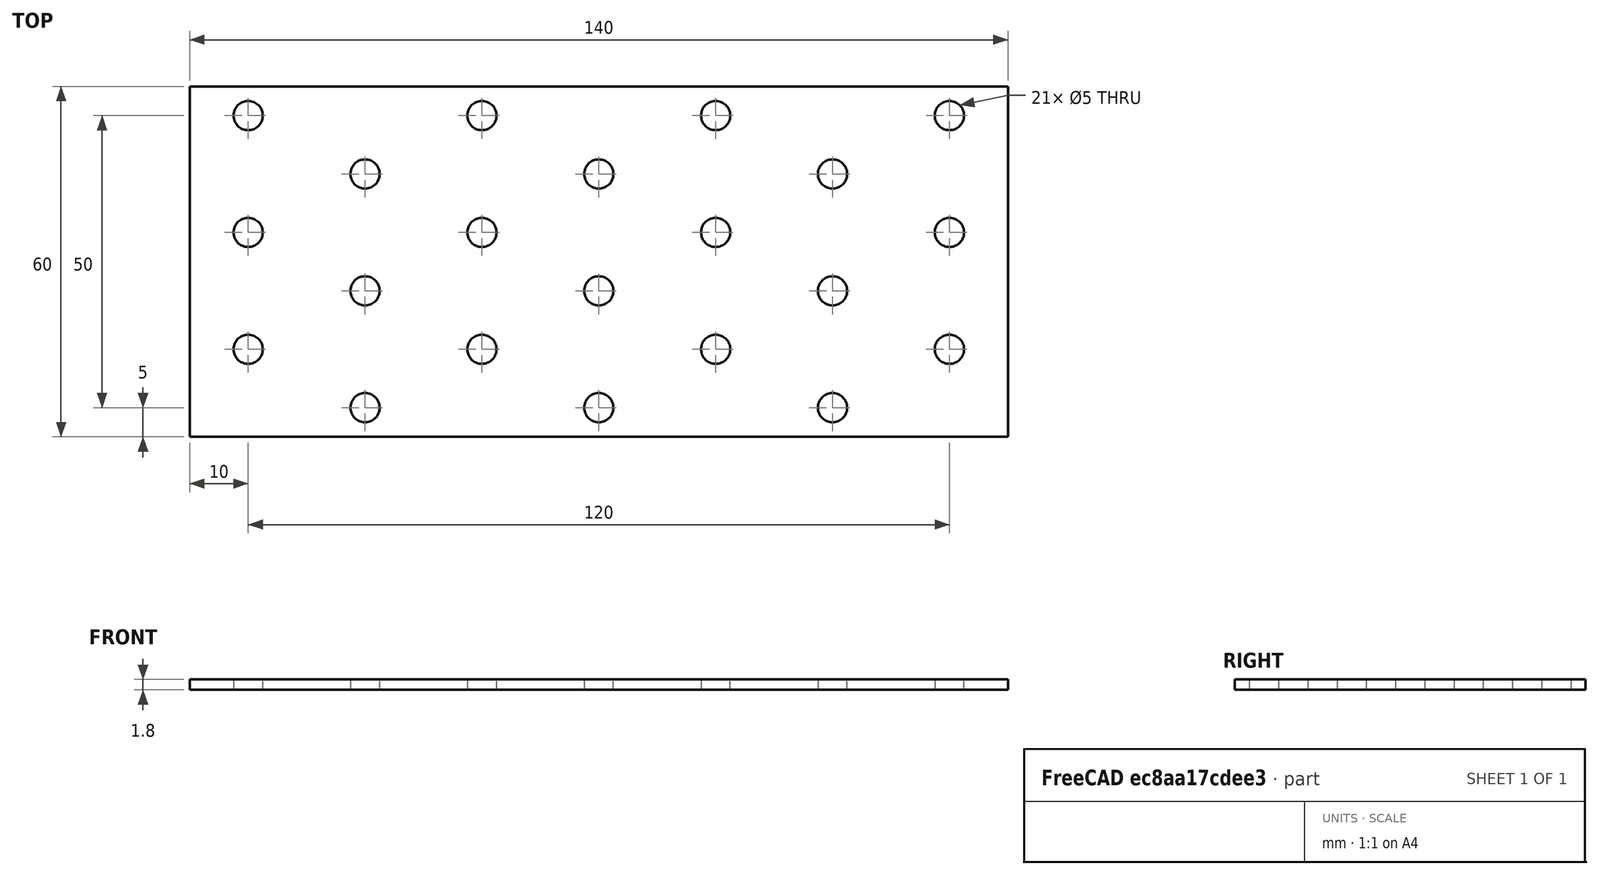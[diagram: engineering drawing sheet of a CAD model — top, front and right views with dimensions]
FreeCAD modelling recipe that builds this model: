
FCSTD DOCUMENT  (FreeCAD 0.19R24276 (Git))
Label: Bar_60x140__1_8mm_for-kern_endpoint_plate
License: All rights reserved
LicenseURL: http://en.wikipedia.org/wiki/All_rights_reserved
objects: Sketcher::SketchObject×1, PartDesign::Pad×1, PartDesign::Body×1
note: 4 computed .brp shape members not serialized (recipe doc carries the construction recipe); baked Part::Feature solids carry a one-line shape summary decoded from their .brp

FEATURE [Sketcher::SketchObject] Sketch
  FullyConstrained = false
  MapMode = 5
  Support = -> [XY_Plane]
  sketch-geometry (56):
    g0: LineSegment StartX=0 StartY=0 StartZ=0 EndX=120 EndY=0 EndZ=0
    g1: LineSegment StartX=120 StartY=0 StartZ=0 EndX=120 EndY=80 EndZ=0
    g2: LineSegment StartX=120 StartY=80 StartZ=0 EndX=0 EndY=80 EndZ=0
    g3: LineSegment StartX=0 StartY=80 StartZ=0 EndX=0 EndY=0 EndZ=0
    g4: LineSegment StartX=0 StartY=4.5 StartZ=0 EndX=120 EndY=4.5 EndZ=0
    g5: LineSegment StartX=0 StartY=24.5 StartZ=0 EndX=120 EndY=24.5 EndZ=0
    g6: LineSegment StartX=0 StartY=44.5 StartZ=0 EndX=120 EndY=44.5 EndZ=0
    g7: LineSegment StartX=0 StartY=64.5 StartZ=0 EndX=120 EndY=64.5 EndZ=0
    g8: LineSegment StartX=48.5 StartY=0 StartZ=0 EndX=48.5 EndY=4.5 EndZ=0
    g9: LineSegment StartX=68.5 StartY=0 StartZ=0 EndX=68.5 EndY=4.5 EndZ=0
    g10: LineSegment StartX=88.5 StartY=0 StartZ=0 EndX=88.5 EndY=4.5 EndZ=0
    g11: LineSegment StartX=108.5 StartY=0 StartZ=0 EndX=108.5 EndY=4.5 EndZ=0
    g12: LineSegment StartX=0 StartY=14.5 StartZ=0 EndX=120 EndY=14.5 EndZ=0
    g13: LineSegment StartX=0 StartY=34.5 StartZ=0 EndX=120 EndY=34.5 EndZ=0
    g14: LineSegment StartX=0 StartY=54.5 StartZ=0 EndX=120 EndY=54.5 EndZ=0
    g15: LineSegment StartX=0 StartY=74.5 StartZ=0 EndX=120 EndY=74.5 EndZ=0
    g16: LineSegment StartX=48.5 StartY=24.5 StartZ=0 EndX=48.5 EndY=80 EndZ=0
    g17: LineSegment StartX=68.5 StartY=14.5 StartZ=0 EndX=68.5 EndY=80 EndZ=0
    g18: LineSegment StartX=88.5 StartY=24.5 StartZ=0 EndX=88.5 EndY=80 EndZ=0
    g19: LineSegment StartX=108.5 StartY=14.5 StartZ=0 EndX=108.5 EndY=80 EndZ=0
    g20: Circle CenterX=28.5 CenterY=14.5 CenterZ=0 NormalX=0 NormalY=0 NormalZ=1 AngleXU=0 Radius=2.5
    g21: Circle CenterX=108.5 CenterY=14.5 CenterZ=0 NormalX=0 NormalY=0 NormalZ=1 AngleXU=0 Radius=2.5
    g22: Circle CenterX=8.5 CenterY=24.5 CenterZ=0 NormalX=0 NormalY=0 NormalZ=1 AngleXU=0 Radius=2.5
    g23: Circle CenterX=48.5 CenterY=24.5 CenterZ=0 NormalX=0 NormalY=0 NormalZ=1 AngleXU=0 Radius=2.5
    g24: Circle CenterX=88.5 CenterY=24.5 CenterZ=0 NormalX=0 NormalY=0 NormalZ=1 AngleXU=0 Radius=2.5
    g25: Circle CenterX=8.5 CenterY=44.5 CenterZ=0 NormalX=0 NormalY=0 NormalZ=1 AngleXU=0 Radius=2.5
    g26: Circle CenterX=48.5 CenterY=44.5 CenterZ=0 NormalX=0 NormalY=0 NormalZ=1 AngleXU=0 Radius=2.5
    g27: Circle CenterX=88.5 CenterY=44.5 CenterZ=0 NormalX=0 NormalY=0 NormalZ=1 AngleXU=0 Radius=2.5
    g28: Circle CenterX=28.5 CenterY=54.5 CenterZ=0 NormalX=0 NormalY=0 NormalZ=1 AngleXU=0 Radius=2.5
    g29: Circle CenterX=68.5 CenterY=54.5 CenterZ=0 NormalX=0 NormalY=0 NormalZ=1 AngleXU=0 Radius=2.5
    g30: Circle CenterX=108.5 CenterY=54.5 CenterZ=0 NormalX=0 NormalY=0 NormalZ=1 AngleXU=0 Radius=2.5
    g31: Circle CenterX=88.5 CenterY=64.5 CenterZ=0 NormalX=0 NormalY=0 NormalZ=1 AngleXU=0 Radius=2.5
    g32: Circle CenterX=48.5 CenterY=64.5 CenterZ=0 NormalX=0 NormalY=0 NormalZ=1 AngleXU=0 Radius=2.5
    g33: Circle CenterX=8.5 CenterY=64.5 CenterZ=0 NormalX=0 NormalY=0 NormalZ=1 AngleXU=0 Radius=2.5
    g34: Circle CenterX=28.5 CenterY=34.5 CenterZ=0 NormalX=0 NormalY=0 NormalZ=1 AngleXU=0 Radius=2.5
    g35: Circle CenterX=68.5 CenterY=34.5 CenterZ=0 NormalX=0 NormalY=0 NormalZ=1 AngleXU=0 Radius=2.5
    g36: Circle CenterX=108.5 CenterY=34.5 CenterZ=0 NormalX=0 NormalY=0 NormalZ=1 AngleXU=0 Radius=2.5
    g37: LineSegment StartX=28.5 StartY=74.5 StartZ=0 EndX=28.5 EndY=14.5 EndZ=0
    g38: LineSegment StartX=8.5 StartY=4.5 StartZ=0 EndX=8.5 EndY=24.5 EndZ=0
    g39: Circle CenterX=68.5 CenterY=14.5 CenterZ=0 NormalX=0 NormalY=0 NormalZ=1 AngleXU=0 Radius=2.5
    g40: LineSegment StartX=-1.5 StartY=9.5 StartZ=0 EndX=136.864 EndY=9.5 EndZ=0
    g41: LineSegment StartX=-1.5 StartY=69.5 StartZ=0 EndX=136.864 EndY=69.5 EndZ=0
    g42: LineSegment StartX=-1.5 StartY=69.5 StartZ=0 EndX=-1.5 EndY=9.5 EndZ=0
    g43: LineSegment StartX=136.864 StartY=69.5 StartZ=0 EndX=136.864 EndY=9.5 EndZ=0
    g44: Circle CenterX=128.5 CenterY=24.5 CenterZ=0 NormalX=0 NormalY=0 NormalZ=1 AngleXU=0 Radius=2.5
    g45: Circle CenterX=128.5 CenterY=44.5 CenterZ=0 NormalX=0 NormalY=0 NormalZ=1 AngleXU=0 Radius=2.5
    g46: Circle CenterX=128.5 CenterY=64.5 CenterZ=0 NormalX=0 NormalY=0 NormalZ=1 AngleXU=0 Radius=2.5
    g47: LineSegment StartX=172.191 StartY=-32.1651 StartZ=0 EndX=159.254 EndY=-63.3642 EndZ=0
    g48: LineSegment StartX=159.254 StartY=-63.3642 StartZ=0 EndX=192.742 EndY=-58.9685 EndZ=0
    g49: LineSegment StartX=192.742 StartY=-58.9685 StartZ=0 EndX=172.191 EndY=-32.1651 EndZ=0
    g50: Circle CenterX=174.729 CenterY=-51.4993 CenterZ=0 NormalX=0 NormalY=0 NormalZ=1 AngleXU=0 Radius=19.5
    g51: Circle CenterX=172.191 CenterY=-32.1651 CenterZ=0 NormalX=0 NormalY=0 NormalZ=1 AngleXU=0 Radius=1
    g52: Circle CenterX=159.254 CenterY=-63.3642 CenterZ=0 NormalX=0 NormalY=0 NormalZ=1 AngleXU=0 Radius=1
    g53: Circle CenterX=192.742 CenterY=-58.9685 CenterZ=0 NormalX=0 NormalY=0 NormalZ=1 AngleXU=0 Radius=1
    g54: Circle CenterX=174.729 CenterY=-51.4993 CenterZ=0 NormalX=0 NormalY=0 NormalZ=1 AngleXU=0 Radius=1
    g55: Circle CenterX=67.6819 CenterY=39.5 CenterZ=0 NormalX=0 NormalY=0 NormalZ=1 AngleXU=0 Radius=1.5
  constraints (119):
    c: Coincident(g0,g1)
    c: Coincident(g1,g2)
    c: Coincident(g2,g3)
    c: Coincident(g3,g0)
    c: Horizontal(g0)
    c: Horizontal(g2)
    c: Vertical(g1)
    c: Vertical(g3)
    c: Coincident(g0,g-1)
    c: DistanceX(g0,g0) = 120
    c: DistanceY(g3,g3) = 80
    c: Horizontal(g4)
    c: PointOnObject(g4,g3)
    c: PointOnObject(g4,g1)
    c: Horizontal(g5)
    c: PointOnObject(g5,g3)
    c: PointOnObject(g5,g1)
    c: DistanceY(g4,g5) = 20
    c: Horizontal(g6)
    c: PointOnObject(g6,g1)
    c: PointOnObject(g6,g3)
    c: DistanceY(g5,g6) = 20
    c: Horizontal(g7)
    c: PointOnObject(g7,g1)
    c: PointOnObject(g7,g3)
    c: DistanceY(g6,g7) = 20
    c: Vertical(g8)
    c: Vertical(g9)
    c: Vertical(g10)
    c: Vertical(g11)
    c: PointOnObject(g8,g0)
    c: PointOnObject(g9,g0)
    c: PointOnObject(g10,g0)
    c: PointOnObject(g11,g0)
    c: PointOnObject(g19,g2)
    c: PointOnObject(g18,g2)
    c: PointOnObject(g17,g2)
    c: PointOnObject(g16,g2)
    c: DistanceX(g8,g9) = 20
    c: DistanceX(g9,g10) = 20
    c: DistanceX(g10,g11) = 20
    c: Horizontal(g12)
    c: Horizontal(g13)
    c: Horizontal(g14)
    c: Horizontal(g15)
    c: PointOnObject(g12,g3)
    c: PointOnObject(g13,g3)
    c: PointOnObject(g14,g3)
    c: PointOnObject(g15,g3)
    c: PointOnObject(g15,g1)
    c: PointOnObject(g14,g1)
    c: PointOnObject(g13,g1)
    c: PointOnObject(g12,g1)
    c: DistanceY(g0,g12) = 14.5
    c: DistanceY(g12,g13) = 20
    c: DistanceY(g13,g14) = 20
    c: DistanceY(g14,g15) = 20
    c: PointOnObject(g20,g12)
    c: PointOnObject(g8,g4)
    c: Tangent(g8,g16)
    c: PointOnObject(g9,g4)
    c: PointOnObject(g17,g12)
    c: Tangent(g9,g17)
    c: PointOnObject(g10,g4)
    c: Tangent(g10,g18)
    c: PointOnObject(g11,g4)
    c: PointOnObject(g19,g12)
    c: Tangent(g11,g19)
    c: Coincident(g21,g19)
    c: Diameter(g20) = 5
    c: PointOnObject(g16,g5)
    c: PointOnObject(g18,g5)
    c: Equal(g23,g24)
    c: Equal(g33,g28)
    c: Equal(g28,g32)
    c: Equal(g32,g31)
    c: Equal(g31,g30)
    c: Diameter(g28) = 5
    c: Equal(g31,g29)
    c: Equal(g26,g27)
    c: Diameter(g34) = 5
    c: Coincident(g37,g20)
    c: Vertical(g37)
    c: DistanceY(g0,g4) = 4.5
    c: Coincident(g38,g22)
    c: Vertical(g38)
    c: Coincident(g39,g17)
    c: Equal(g21,g39)
    c: Horizontal(g40)
    c: Horizontal(g41)
    c: Vertical(g42)
    c: DistanceX(g0,g38) = 8.5
    c: Coincident(g42,g40)
    c: Coincident(g41,g42)
    c: Vertical(g43)
    c: DistanceX(g40,g38) = 10
    c: Coincident(g40,g43)
    c: DistanceY(g40,g21) = 5
    c: Coincident(g41,g43)
    c: DistanceY(g40,g41) = 60
    c: Coincident(g47,g48)
    c: Coincident(g48,g49)
    c: Coincident(g49,g47)
    c: Equal(g47,g48)
    c: Equal(g47,g49)
    c: PointOnObject(g47,g50)
    c: PointOnObject(g48,g50)
    c: PointOnObject(g49,g50)
    c: Diameter(g50) = 39
    c: Coincident(g51,g47)
    c: Coincident(g52,g47)
    c: Coincident(g53,g48)
    c: Diameter(g51) = 2
    c: Equal(g51,g52)
    c: Equal(g51,g53)
    c: Coincident(g54,g50)
    c: Diameter(g54) = 2
    c: Symmetric(g40,g41,g55)
    c: Diameter(g55) = 3
FEATURE [PartDesign::Pad] Pad
  Direction = (1,1,1)
  Length = 1.8
  Length2 = 100
  Profile = -> Sketch
  Type = 0
FEATURE [PartDesign::Body] Body
  Group = -> [Sketch,Pad]
  Origin = -> Origin
  Tip = -> Pad
